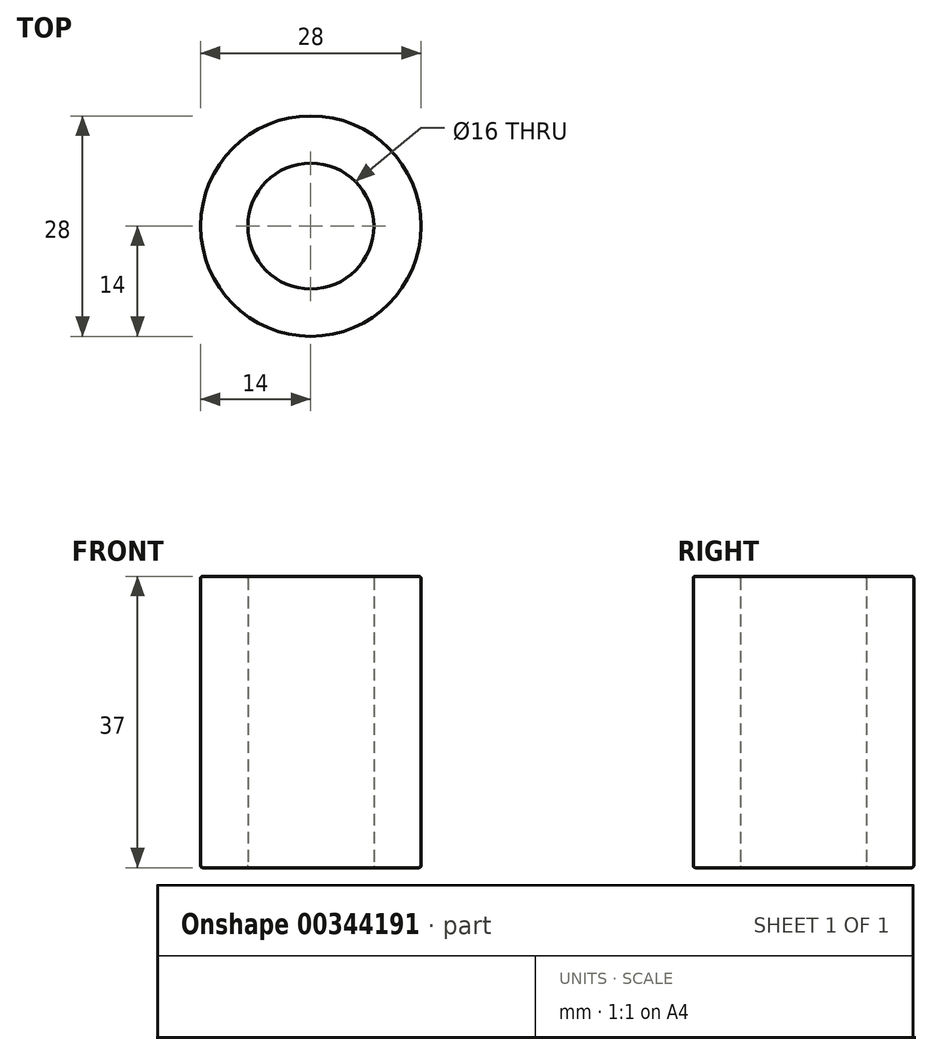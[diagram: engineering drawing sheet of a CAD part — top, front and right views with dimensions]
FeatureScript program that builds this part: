
annotation { "Feature Type Name" : "Feature", "Feature Type Description" : "" }
export const myFeature = defineFeature(function(context is Context, id is Id, definition is map)
    precondition{}
    {
        {
            var Q0;
            Q0=qCreatedBy(makeId("Top.planeOp"),FACE);
            var sketch = newSketch(context, id + "F0", { "sketchPlane" : qUnion([Q0])});
            skCircle(sketch, "E0", {"center": v(0, 0) * mm, "radius": 8 * mm});
            skCircle(sketch, "E1", {"center": v(0, 0) * mm, "radius": 14 * mm});
            skSolve(sketch);
        }
        {
            var Q0;
            Q0=qSketchRegion(id+"F0",true);
            extrude(context, id + "F1", {"entities" : qUnion([Q0]), "depth" : 37 * mm});
        }
        {
            var Q0;
            Q0=makeQuery(id+"F1.opExtrude","CAP_FACE",FACE,{"disambiguationData":[OSD([sQuery(id+"F0.wireOp",EDGE,"E0"),sQuery(id+"F0.wireOp",EDGE,"E1")])],"isStart":false});
            var Q1;
            Q1=makeQuery(id+"F1.opExtrude","CAP_FACE",FACE,{"disambiguationData":[OSD([sQuery(id+"F0.wireOp",EDGE,"E0"),sQuery(id+"F0.wireOp",EDGE,"E1")])],"isStart":true});
            fillet(context, id + "F2", {"entities" : qUnion([Q0, Q1]), "radius" : .25 * mm, "tangentPropagation" : true, "allowEdgeOverflow" : false});
        }
    });
